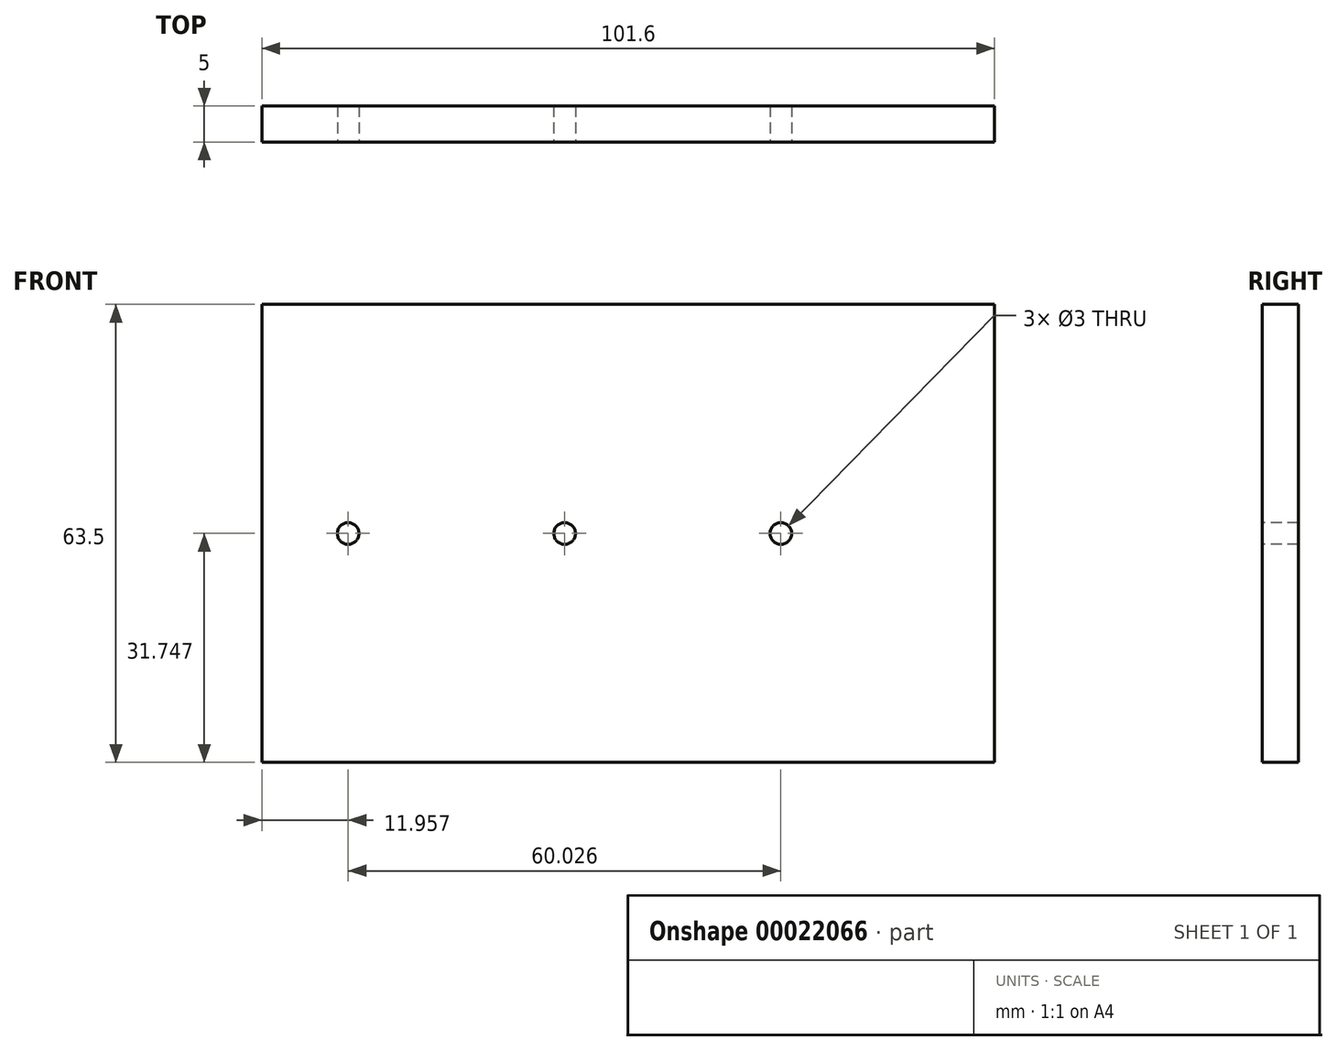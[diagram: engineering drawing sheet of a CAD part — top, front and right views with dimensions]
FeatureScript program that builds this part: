
annotation { "Feature Type Name" : "Feature", "Feature Type Description" : "" }
export const myFeature = defineFeature(function(context is Context, id is Id, definition is map)
    precondition{}
    {
        {
            var Q0;
            Q0=qCreatedBy(makeId("Front.planeOp"),FACE);
            var sketch = newSketch(context, id + "F0", { "sketchPlane" : qUnion([Q0])});
            skLineSegment(sketch, "E0.bottom", {"start": v(-41.15, 38.55) * mm, "end": v(60.45, 38.55) * mm});
            skLineSegment(sketch, "E0.top", {"start": v(-41.15, -24.95) * mm, "end": v(60.45, -24.95) * mm});
            skLineSegment(sketch, "E0.left", {"start": v(-41.15, 38.55) * mm, "end": v(-41.15, -24.95) * mm});
            skLineSegment(sketch, "E0.right", {"start": v(60.45, 38.55) * mm, "end": v(60.45, -24.95) * mm});
            skSolve(sketch);
        }
        {
            var Q0;
            Q0 = qSketchRegion(id + "F0", true);
            extrude(context, id + "F1", {"entities" : qUnion([Q0]), "depth" : 5 * mm});
        }
        {
            var Q0;
            Q0=makeQuery(id+"F1.opExtrude","CAP_FACE",FACE,{"disambiguationData":[OSD([sQuery(id+"F0.wireOp",EDGE,"E0.bottom"),sQuery(id+"F0.wireOp",EDGE,"E0.top"),sQuery(id+"F0.wireOp",EDGE,"E0.left"),sQuery(id+"F0.wireOp",EDGE,"E0.right")])],"isStart":false});
            var sketch = newSketch(context, id + "F2", { "sketchPlane" : qUnion([Q0])});
            skPoint(sketch, "E1", {"position": v(0.84, 6.8) * mm});
            skPoint(sketch, "E2", {"position": v(50.85, 6.8) * mm});
            skCircle(sketch, "E3", {"center": v(0.84, 6.8) * mm, "radius": 1.5 * mm});
            skCircle(sketch, "E4", {"center": v(30.83, 6.8) * mm, "radius": 1.5 * mm});
            skLineSegment(sketch, "E5", {"start": v(0.84, 6.8) * mm, "end": v(-29.2, 6.8) * mm});
            skCircle(sketch, "E6", {"center": v(-29.2, 6.8) * mm, "radius": 1.5 * mm});
            skSolve(sketch);
        }
        {
            var Q0;
            Q0=makeQuery(id+"F2.imprint","IMPRINT",FACE,{"disambiguationData":[TD([[makeQuery(id+"F2.imprint","IMPRINT",EDGE,{"derivedFrom":sQuery(id+"F2.wireOp",EDGE,"E6")}),1.0]])]});
            var Q1;
            Q1=makeQuery(id+"F2.imprint","IMPRINT",FACE,{"disambiguationData":[TD([[makeQuery(id+"F2.imprint","IMPRINT",EDGE,{"derivedFrom":sQuery(id+"F2.wireOp",EDGE,"E3")}),1.0]])]});
            var Q2;
            Q2=makeQuery(id+"F2.imprint","IMPRINT",FACE,{"disambiguationData":[TD([[makeQuery(id+"F2.imprint","IMPRINT",EDGE,{"derivedFrom":sQuery(id+"F2.wireOp",EDGE,"E4")}),1.0]])]});
            extrude(context, id + "F3", {"entities" : qUnion([Q0, Q1, Q2]), "operationType" : NewBodyOperationType.REMOVE, "endBound" : BoundingType.THROUGH_ALL, "oppositeDirection" : true, "depth" : 25.4 * mm});
        }
    });
